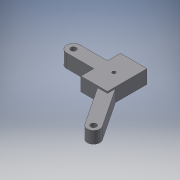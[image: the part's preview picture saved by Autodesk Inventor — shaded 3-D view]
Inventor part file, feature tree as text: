
AUTODESK INVENTOR PART (.ipt)
format: ipt  version: 2017 (Build 210142000, 142)  size: 176,128 bytes
history: native  units: mm
features: extrude x5, sketch x5, projected_geometry x2, plane x1
ambient origin geometry x8: Origin, YZ Plane, XZ Plane, XY Plane, X Axis, Y Axis, Z Axis, Center Point
bodies: Solid1 (feature_tree)
feature tree (13):
  extrude  "Extrusion1"  Depth=19.05mm
  extrude  "Extrusion2"  Depth=10.0mm
  extrude  "Extrusion3"  Depth=10.0mm
  sketch  "Sketch4"  dims[d6=40.0mm d7=15.0mm d8=0.0mm]
  plane  "Work Plane1"
  extrude  "Extrusion4"  Depth=15.0mm TaperAngle=0.0deg
  extrude  "Extrusion5"  Depth=5.0mm
  sketch  "Sketch1"  dims[d0=38.1mm d1=19.05mm]
  sketch  "Sketch2"  dims[d2=10.0mm d3=10.0mm]
  projected_geometry  "Projected Loop1"
  sketch  "Sketch3"  dims[d4=8.0mm d5=10.0mm]
  sketch  "Sketch5"  dims[d9=5.0mm d10=0.0mm d11=5.0mm d12=10.0mm d13=0.0mm d14=80.0mm d15=45.0mm d16=8.5mm d17=10.0mm d18=10.0mm d19=5.0mm d20=10.0mm d21=0.0mm d22=10.0mm d23=0.0mm]
  projected_geometry  "Projected Loop2"
